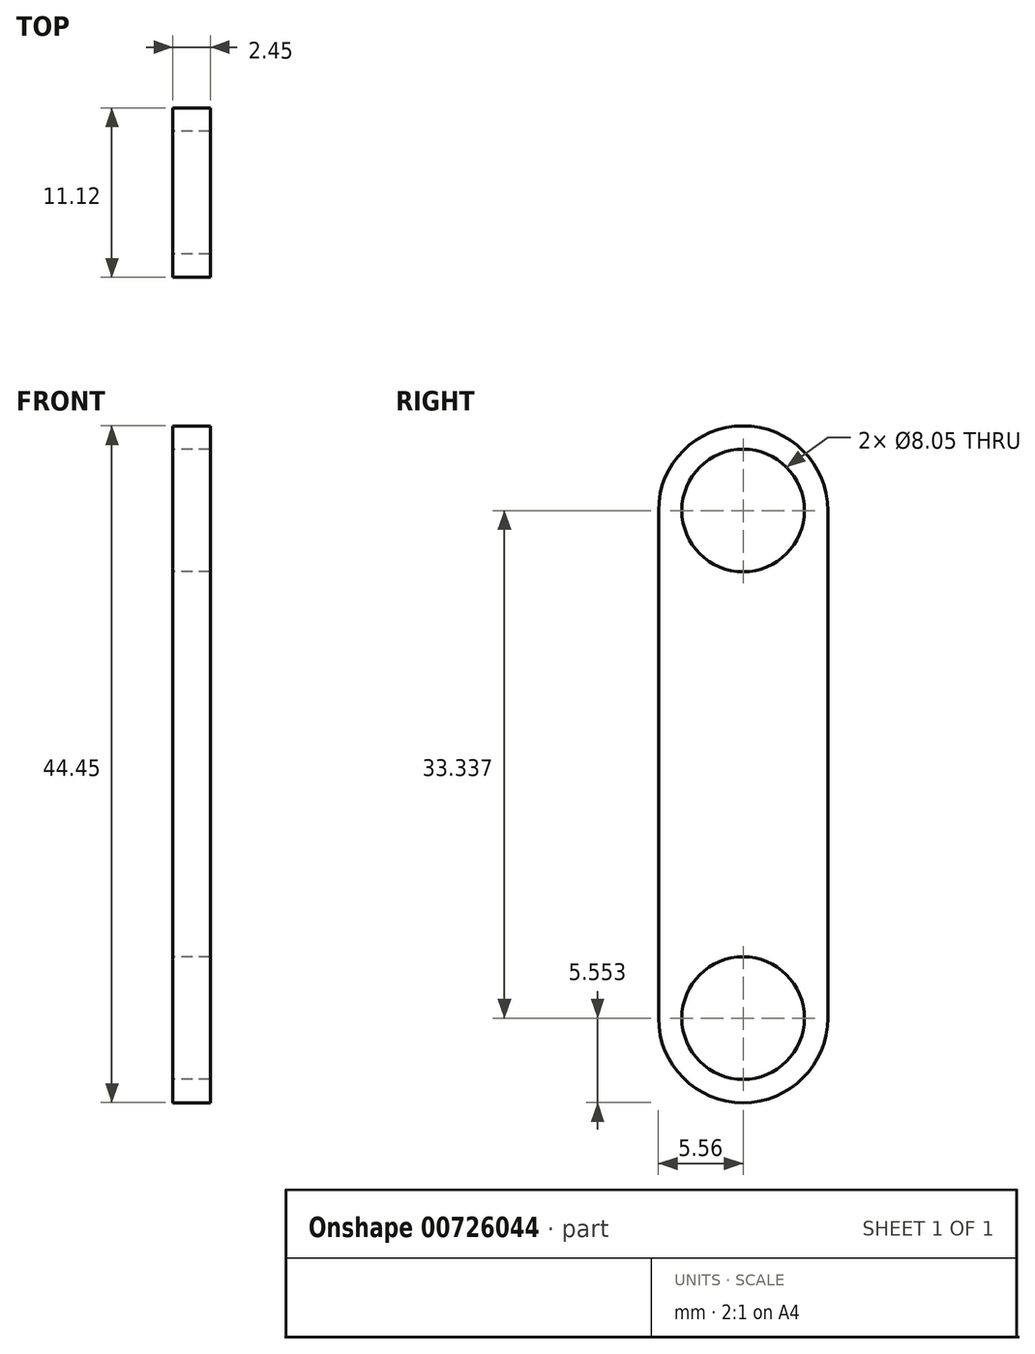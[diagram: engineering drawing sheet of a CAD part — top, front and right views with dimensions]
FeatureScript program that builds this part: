
annotation { "Feature Type Name" : "Feature", "Feature Type Description" : "" }
export const myFeature = defineFeature(function(context is Context, id is Id, definition is map)
    precondition{}
    {
        {
            var Q0;
            Q0=qCreatedBy(makeId("Right.planeOp"),FACE);
            var sketch = newSketch(context, id + "F0", { "sketchPlane" : qUnion([Q0])});
            skCircle(sketch, "E0", {"center": v(0, 0) * mm, "radius": 4.03 * mm});
            skCircle(sketch, "E1", {"center": v(0, -33.34) * mm, "radius": 4.03 * mm});
            skCircle(sketch, "E2", {"center": v(0, 0) * mm, "radius": 5.56 * mm});
            skCircle(sketch, "E3", {"center": v(0, -33.34) * mm, "radius": 5.56 * mm});
            skLineSegment(sketch, "E4", {"start": v(-5.56, 0) * mm, "end": v(-5.56, -33.34) * mm});
            skLineSegment(sketch, "E5", {"start": v(5.56, 0) * mm, "end": v(5.56, -33.34) * mm});
            skSolve(sketch);
        }
        {
            var Q0;
            Q0=makeQuery(id+"F0.imprint","IMPRINT",FACE,{"disambiguationData":[TD([[makeQuery(id+"F0.imprint","IMPRINT",EDGE,{"derivedFrom":sQuery(id+"F0.wireOp",EDGE,"E0")}),-1.0]])]});
            var Q1;
            {var subQ0=sQuery(id+"F0.wireOp",EDGE,"E4");Q1=makeQuery(id+"F0.imprint","IMPRINT",FACE,{"disambiguationData":[TD([[makeQuery(id+"F0.imprint","IMPRINT",EDGE,{"derivedFrom":subQ0}),1.0]])]});}
            var Q2;
            Q2=makeQuery(id+"F0.imprint","IMPRINT",FACE,{"disambiguationData":[TD([[makeQuery(id+"F0.imprint","IMPRINT",EDGE,{"derivedFrom":sQuery(id+"F0.wireOp",EDGE,"E1")}),-1.0]])]});
            extrude(context, id + "F1", {"entities" : qUnion([Q0, Q1, Q2]), "depth" : 2.45 * mm, "offsetDistance" : 25.4 * mm});
        }
    });
